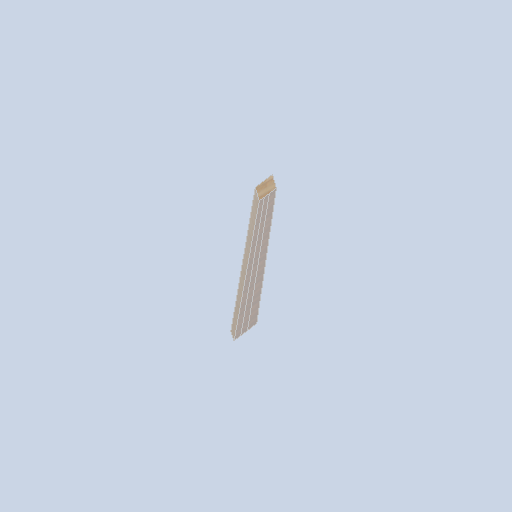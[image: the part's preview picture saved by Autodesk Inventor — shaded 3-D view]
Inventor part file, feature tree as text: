
AUTODESK INVENTOR PART (.ipt)
format: ipt  version: 2024.2 (Build 282272000, 272)  size: 122,880 bytes
history: native  units: in
note: dims shown in document units (in); Inventor stores cm internally (conversion verified against a paired STEP export)
features: sketch x4, other x3, plane x2
ambient origin geometry x8: Origin, YZ Plane, XZ Plane, XY Plane, X Axis, Y Axis, Z Axis, Center Point
bodies: Solid1 (feature_tree)
feature tree (9):
  other  "side_curve_beam_03.ipt"
  other  "Solid1::side_curve_beam_03.ipt"
  other  "TaggingFeature1"
  sketch  "Sketch1"  dims[d0=0.3937in]
  sketch  "Sketch2"
  sketch  "Sketch3"
  sketch  "Sketch4"
  plane  "Work Plane1"
  plane  "Work Plane2"
